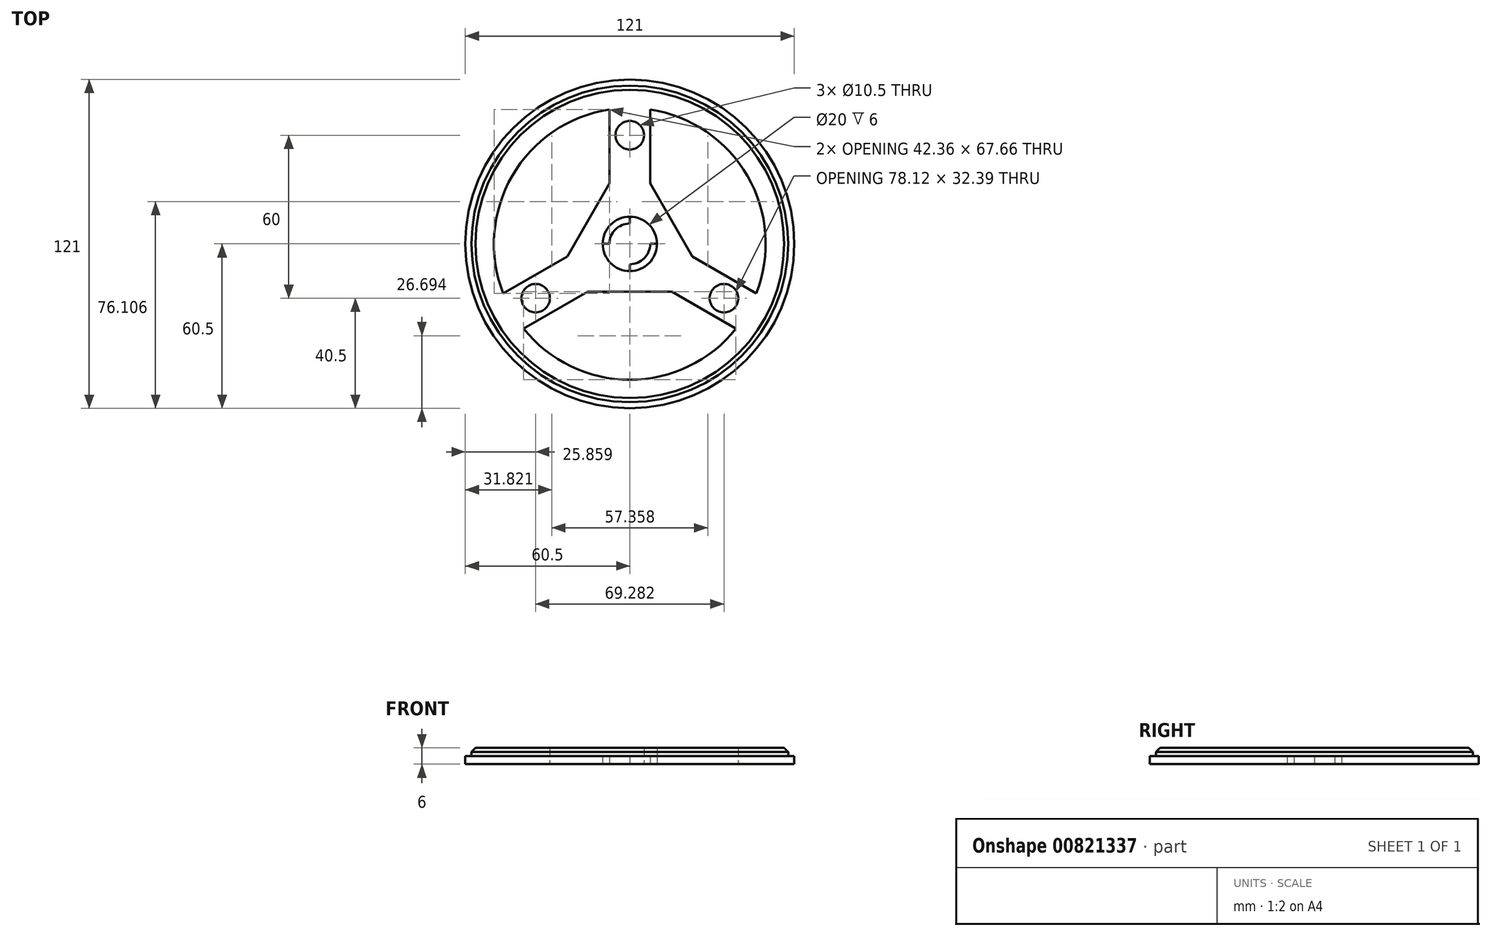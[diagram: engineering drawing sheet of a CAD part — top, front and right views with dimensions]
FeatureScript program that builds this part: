
annotation { "Feature Type Name" : "Feature", "Feature Type Description" : "" }
export const myFeature = defineFeature(function(context is Context, id is Id, definition is map)
    precondition{}
    {
        {
            var Q0;
            Q0=qCreatedBy(makeId("Top.planeOp"),FACE);
            var sketch = newSketch(context, id + "F0", { "sketchPlane" : qUnion([Q0])});
            skCircle(sketch, "E0", {"center": v(0, 0) * mm, "radius": 60.5 * mm});
            skCircle(sketch, "E1", {"center": v(0, 0) * mm, "radius": 50 * mm});
            skCircle(sketch, "E2", {"center": v(0, 0) * mm, "radius": 58.25 * mm});
            skLineSegment(sketch, "E3", {"start": v(0, 50) * mm, "end": v(0, 40) * mm});
            skCircle(sketch, "E4", {"center": v(0, 40) * mm, "radius": 5.25 * mm});
            skCircle(sketch, "E5", {"center": v(0, 40) * mm, "radius": 7.5 * mm});
            skLineSegment(sketch, "E6.bottom", {"start": v(7.5, 57.77) * mm, "end": v(-7.5, 57.77) * mm});
            skLineSegment(sketch, "E6.top", {"start": v(7.5, 22.23) * mm, "end": v(-7.5, 22.23) * mm});
            skLineSegment(sketch, "E6.left", {"start": v(7.5, 57.77) * mm, "end": v(7.5, 22.23) * mm});
            skLineSegment(sketch, "E6.right", {"start": v(-7.5, 57.77) * mm, "end": v(-7.5, 22.23) * mm});
            skCircle(sketch, "E7.1.0", {"center": v(34.64, -20) * mm, "radius": 7.5 * mm});
            skCircle(sketch, "E7.1.1", {"center": v(34.64, -20) * mm, "radius": 5.25 * mm});
            skLineSegment(sketch, "E7.1.2", {"start": v(53.78, -22.39) * mm, "end": v(23, -4.62) * mm});
            skLineSegment(sketch, "E7.1.3", {"start": v(46.28, -35.38) * mm, "end": v(15.5, -17.61) * mm});
            skCircle(sketch, "E7.2.0", {"center": v(-34.64, -20) * mm, "radius": 7.5 * mm});
            skCircle(sketch, "E7.2.1", {"center": v(-34.64, -20) * mm, "radius": 5.25 * mm});
            skLineSegment(sketch, "E7.2.2", {"start": v(-46.28, -35.38) * mm, "end": v(-15.5, -17.61) * mm});
            skLineSegment(sketch, "E7.2.3", {"start": v(-53.78, -22.39) * mm, "end": v(-23, -4.62) * mm});
            skLineSegment(sketch, "E7.anchor1", {"start": v(0, 0) * mm, "end": v(0, 40) * mm, "construction": true});
            skLineSegment(sketch, "E7.anchor2", {"start": v(0, 0) * mm, "end": v(-34.64, -20) * mm, "construction": true});
            skCircle(sketch, "E8", {"center": v(0, 40) * mm, "radius": 3.5 * mm});
            skCircle(sketch, "E9", {"center": v(-34.64, -20) * mm, "radius": 3.5 * mm});
            skCircle(sketch, "E10", {"center": v(34.64, -20) * mm, "radius": 3.5 * mm});
            skLineSegment(sketch, "E11", {"start": v(-23, -4.62) * mm, "end": v(-7.5, 22.23) * mm});
            skLineSegment(sketch, "E12", {"start": v(7.5, 22.23) * mm, "end": v(23, -4.62) * mm});
            skLineSegment(sketch, "E13", {"start": v(15.5, -17.61) * mm, "end": v(-15.5, -17.61) * mm});
            skCircle(sketch, "E14", {"center": v(0, 0) * mm, "radius": 7.5 * mm});
            skCircle(sketch, "E15", {"center": v(0, 0) * mm, "radius": 10 * mm});
            skLineSegment(sketch, "E16", {"start": v(0, -10) * mm, "end": v(0, 10) * mm});
            skLineSegment(sketch, "E17", {"start": v(-10, 0) * mm, "end": v(10, 0) * mm});
            skSolve(sketch);
        }
        {
            var Q0;
            {var subQ0=sQuery(id+"F0.wireOp",EDGE,"E6.left");var subQ1=sQuery(id+"F0.wireOp",EDGE,"E1");var subQ2=makeQuery(id+"F0.imprint","INTERSECT",VERTEX,{"derivedFrom":[subQ1,subQ0]});Q0=makeQuery(id+"F0.imprint","IMPRINT",FACE,{"disambiguationData":[TD([[makeQuery(id+"F0.imprint","IMPRINT",EDGE,{"disambiguationData":[TD([[subQ2,1.0]])],"derivedFrom":subQ1}),-1.0]])]});}
            var Q1;
            {var subQ0=sQuery(id+"F0.wireOp",EDGE,"E6.bottom");Q1=makeQuery(id+"F0.imprint","IMPRINT",FACE,{"disambiguationData":[TD([[makeQuery(id+"F0.imprint","IMPRINT",EDGE,{"derivedFrom":subQ0}),1.0]])]});}
            var Q2;
            {var subQ0=sQuery(id+"F0.wireOp",EDGE,"E6.right");var subQ1=sQuery(id+"F0.wireOp",EDGE,"E1");var subQ2=makeQuery(id+"F0.imprint","INTERSECT",VERTEX,{"derivedFrom":[subQ1,subQ0]});Q2=makeQuery(id+"F0.imprint","IMPRINT",FACE,{"disambiguationData":[TD([[makeQuery(id+"F0.imprint","IMPRINT",EDGE,{"disambiguationData":[TD([[subQ2,-1.0]])],"derivedFrom":subQ1}),-1.0]])]});}
            var Q3;
            {var subQ0=sQuery(id+"F0.wireOp",EDGE,"E7.2.3");var subQ1=sQuery(id+"F0.wireOp",EDGE,"E1");var subQ2=makeQuery(id+"F0.imprint","INTERSECT",VERTEX,{"derivedFrom":[subQ1,subQ0]});Q3=makeQuery(id+"F0.imprint","IMPRINT",FACE,{"disambiguationData":[TD([[makeQuery(id+"F0.imprint","IMPRINT",EDGE,{"disambiguationData":[TD([[subQ2,-1.0]])],"derivedFrom":subQ1}),-1.0]])]});}
            var Q4;
            {var subQ0=sQuery(id+"F0.wireOp",EDGE,"E7.2.2");var subQ1=sQuery(id+"F0.wireOp",EDGE,"E1");var subQ2=makeQuery(id+"F0.imprint","INTERSECT",VERTEX,{"derivedFrom":[subQ1,subQ0]});Q4=makeQuery(id+"F0.imprint","IMPRINT",FACE,{"disambiguationData":[TD([[makeQuery(id+"F0.imprint","IMPRINT",EDGE,{"disambiguationData":[TD([[subQ2,-1.0]])],"derivedFrom":subQ1}),-1.0]])]});}
            var Q5;
            {var subQ0=sQuery(id+"F0.wireOp",EDGE,"E7.1.3");var subQ1=sQuery(id+"F0.wireOp",EDGE,"E1");var subQ2=makeQuery(id+"F0.imprint","INTERSECT",VERTEX,{"derivedFrom":[subQ1,subQ0]});Q5=makeQuery(id+"F0.imprint","IMPRINT",FACE,{"disambiguationData":[TD([[makeQuery(id+"F0.imprint","IMPRINT",EDGE,{"disambiguationData":[TD([[subQ2,-1.0]])],"derivedFrom":subQ1}),-1.0]])]});}
            var Q6;
            {var subQ0=sQuery(id+"F0.wireOp",EDGE,"E6.bottom");Q6=makeQuery(id+"F0.imprint","IMPRINT",FACE,{"disambiguationData":[TD([[makeQuery(id+"F0.imprint","IMPRINT",EDGE,{"derivedFrom":subQ0}),-1.0]])]});}
            var Q7;
            {var subQ0=sQuery(id+"F0.wireOp",EDGE,"E3");var subQ1=sQuery(id+"F0.wireOp",EDGE,"E1");var subQ2=makeQuery(id+"F0.imprint","INTERSECT",VERTEX,{"derivedFrom":[subQ1,subQ0]});Q7=makeQuery(id+"F0.imprint","IMPRINT",FACE,{"disambiguationData":[TD([[makeQuery(id+"F0.imprint","IMPRINT",EDGE,{"disambiguationData":[TD([[subQ2,1.0]])],"derivedFrom":subQ1}),1.0]])]});}
            var Q8;
            {var subQ0=sQuery(id+"F0.wireOp",EDGE,"E3");var subQ1=sQuery(id+"F0.wireOp",EDGE,"E1");var subQ2=makeQuery(id+"F0.imprint","INTERSECT",VERTEX,{"derivedFrom":[subQ1,subQ0]});Q8=makeQuery(id+"F0.imprint","IMPRINT",FACE,{"disambiguationData":[TD([[makeQuery(id+"F0.imprint","IMPRINT",EDGE,{"disambiguationData":[TD([[subQ2,-1.0]])],"derivedFrom":subQ1}),1.0]])]});}
            var Q9;
            Q9=makeQuery(id+"F0.imprint","IMPRINT",FACE,{"disambiguationData":[TD([[makeQuery(id+"F0.imprint","IMPRINT",EDGE,{"derivedFrom":sQuery(id+"F0.wireOp",EDGE,"E4")}),-1.0]])]});
            var Q10;
            {var subQ0=sQuery(id+"F0.wireOp",EDGE,"E7.1.3");var subQ1=sQuery(id+"F0.wireOp",EDGE,"E1");var subQ2=makeQuery(id+"F0.imprint","INTERSECT",VERTEX,{"derivedFrom":[subQ1,subQ0]});Q10=makeQuery(id+"F0.imprint","IMPRINT",FACE,{"disambiguationData":[TD([[makeQuery(id+"F0.imprint","IMPRINT",EDGE,{"disambiguationData":[TD([[subQ2,-1.0]])],"derivedFrom":subQ1}),1.0]])]});}
            var Q11;
            Q11=makeQuery(id+"F0.imprint","IMPRINT",FACE,{"disambiguationData":[TD([[makeQuery(id+"F0.imprint","IMPRINT",EDGE,{"derivedFrom":sQuery(id+"F0.wireOp",EDGE,"E7.1.1")}),-1.0]])]});
            var Q12;
            Q12=makeQuery(id+"F0.imprint","IMPRINT",FACE,{"disambiguationData":[TD([[makeQuery(id+"F0.imprint","IMPRINT",EDGE,{"derivedFrom":sQuery(id+"F0.wireOp",EDGE,"E7.2.1")}),-1.0]])]});
            var Q13;
            {var subQ0=sQuery(id+"F0.wireOp",EDGE,"E7.2.3");var subQ1=sQuery(id+"F0.wireOp",EDGE,"E1");var subQ2=makeQuery(id+"F0.imprint","INTERSECT",VERTEX,{"derivedFrom":[subQ1,subQ0]});Q13=makeQuery(id+"F0.imprint","IMPRINT",FACE,{"disambiguationData":[TD([[makeQuery(id+"F0.imprint","IMPRINT",EDGE,{"disambiguationData":[TD([[subQ2,-1.0]])],"derivedFrom":subQ1}),1.0]])]});}
            var Q14;
            {var subQ5=sQuery(id+"F0.wireOp",EDGE,"E6.top");Q14=makeQuery(id+"F0.imprint","IMPRINT",FACE,{"disambiguationData":[TD([[makeQuery(id+"F0.imprint","IMPRINT",EDGE,{"derivedFrom":subQ5}),-1.0]])]});}
            var Q15;
            Q15=makeQuery(id+"F0.imprint","IMPRINT",FACE,{"disambiguationData":[TD([[makeQuery(id+"F0.imprint","IMPRINT",EDGE,{"derivedFrom":sQuery(id+"F0.wireOp",EDGE,"E6.top")}),1.0]])]});
            extrude(context, id + "F1", {"entities" : qUnion([Q0, Q1, Q2, Q3, Q4, Q5, Q6, Q7, Q8, Q9, Q10, Q11, Q12, Q13, Q14, Q15]), "depth" : 6 * mm, "offsetDistance" : 25 * mm});
        }
        {
            var Q0;
            Q0=makeQuery(id+"F0.imprint","IMPRINT",FACE,{"disambiguationData":[TD([[makeQuery(id+"F0.imprint","IMPRINT",EDGE,{"derivedFrom":sQuery(id+"F0.wireOp",EDGE,"E0")}),1.0]])]});
            var Q1;
            {var subQ0=sQuery(id+"F0.wireOp",EDGE,"E16");var subQ1=sQuery(id+"F0.wireOp",EDGE,"E14");var subQ2=makeQuery(id+"F0.imprint","INTERSECT",VERTEX,{"disambiguationData":[OD(0.0)],"derivedFrom":[subQ1,subQ0]});Q1=makeQuery(id+"F0.imprint","IMPRINT",FACE,{"disambiguationData":[TD([[makeQuery(id+"F0.imprint","IMPRINT",EDGE,{"disambiguationData":[TD([[subQ2,-1.0]])],"derivedFrom":subQ1}),-1.0]])]});}
            var Q2;
            {var subQ0=sQuery(id+"F0.wireOp",EDGE,"E17");var subQ1=sQuery(id+"F0.wireOp",EDGE,"E14");var subQ2=makeQuery(id+"F0.imprint","INTERSECT",VERTEX,{"disambiguationData":[OD(0.0)],"derivedFrom":[subQ1,subQ0]});Q2=makeQuery(id+"F0.imprint","IMPRINT",FACE,{"disambiguationData":[TD([[makeQuery(id+"F0.imprint","IMPRINT",EDGE,{"disambiguationData":[TD([[subQ2,1.0]])],"derivedFrom":subQ1}),-1.0]])]});}
            extrude(context, id + "F2", {"entities" : qUnion([Q0, Q1, Q2]), "operationType" : NewBodyOperationType.ADD, "depth" : 3 * mm, "offsetDistance" : 25 * mm});
        }
        {
            var Q0;
            Q0=makeQuery(id+"F1.opExtrude","CAP_EDGE",EDGE,{"disambiguationData":[OSD([sQuery(id+"F0.wireOp",EDGE,"E2")])],"isStart":false});
            chamfer(context, id + "F3", {"entities" : qUnion([Q0]), "width" : 1.5 * mm, "tangentPropagation" : true});
        }
    });
